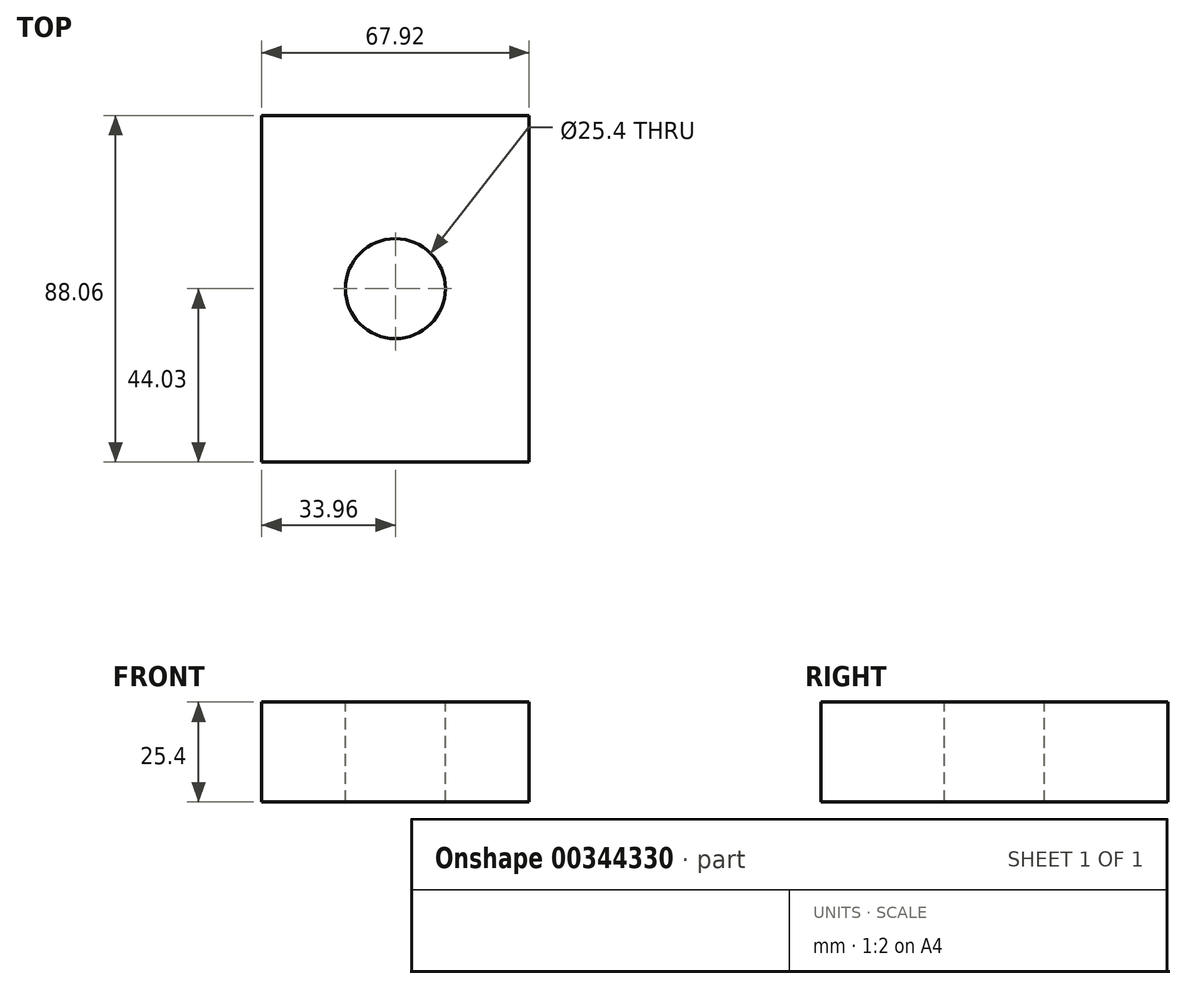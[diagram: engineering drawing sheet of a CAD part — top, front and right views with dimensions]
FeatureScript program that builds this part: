
annotation { "Feature Type Name" : "Feature", "Feature Type Description" : "" }
export const myFeature = defineFeature(function(context is Context, id is Id, definition is map)
    precondition{}
    {
        {
            var Q0;
            Q0=qCreatedBy(makeId("Top.planeOp"),FACE);
            var sketch = newSketch(context, id + "F0", { "sketchPlane" : qUnion([Q0])});
            skLineSegment(sketch, "E0.bottom", {"start": v(33.96, 44.03) * mm, "end": v(-33.96, 44.03) * mm});
            skLineSegment(sketch, "E0.top", {"start": v(33.96, -44.03) * mm, "end": v(-33.96, -44.03) * mm});
            skLineSegment(sketch, "E0.left", {"start": v(33.96, 44.03) * mm, "end": v(33.96, -44.03) * mm});
            skLineSegment(sketch, "E0.right", {"start": v(-33.96, 44.03) * mm, "end": v(-33.96, -44.03) * mm});
            skPoint(sketch, "E0.middle", {"position": v(0, 0) * mm});
            skSolve(sketch);
        }
        {
            var Q0;
            Q0=makeQuery(id+"F0.imprint","IMPRINT",FACE,{"disambiguationData":[TD([[makeQuery(id+"F0.imprint","IMPRINT",EDGE,{"derivedFrom":sQuery(id+"F0.wireOp",EDGE,"E0.bottom")}),1.0]])]});
            extrude(context, id + "F1", {"entities" : qUnion([Q0]), "depth" : 25.4 * mm});
        }
        {
            var Q0;
            Q0=makeQuery(id+"F1.opExtrude","CAP_FACE",FACE,{"disambiguationData":[OSD([sQuery(id+"F0.wireOp",EDGE,"E0.bottom"),sQuery(id+"F0.wireOp",EDGE,"E0.top"),sQuery(id+"F0.wireOp",EDGE,"E0.left"),sQuery(id+"F0.wireOp",EDGE,"E0.right")])],"isStart":false});
            var sketch = newSketch(context, id + "F2", { "sketchPlane" : qUnion([Q0])});
            skCircle(sketch, "E1", {"center": v(0, 0) * mm, "radius": 12.7 * mm});
            skSolve(sketch);
        }
        {
            var Q0;
            Q0 = qSketchRegion(id + "F2", true);
            extrude(context, id + "F3", {"entities" : qUnion([Q0]), "operationType" : NewBodyOperationType.REMOVE, "oppositeDirection" : true, "depth" : 25.4 * mm});
        }
        {
            var Q0;
            Q0=makeQuery(id+"F0.imprint","IMPRINT",FACE,{"disambiguationData":[TD([[makeQuery(id+"F0.imprint","IMPRINT",EDGE,{"derivedFrom":sQuery(id+"F0.wireOp",EDGE,"E0.bottom")}),1.0]])]});
            extrude(context, id + "F4", {"entities" : qUnion([Q0]), "depth" : 25.4 * mm});
        }
    });
